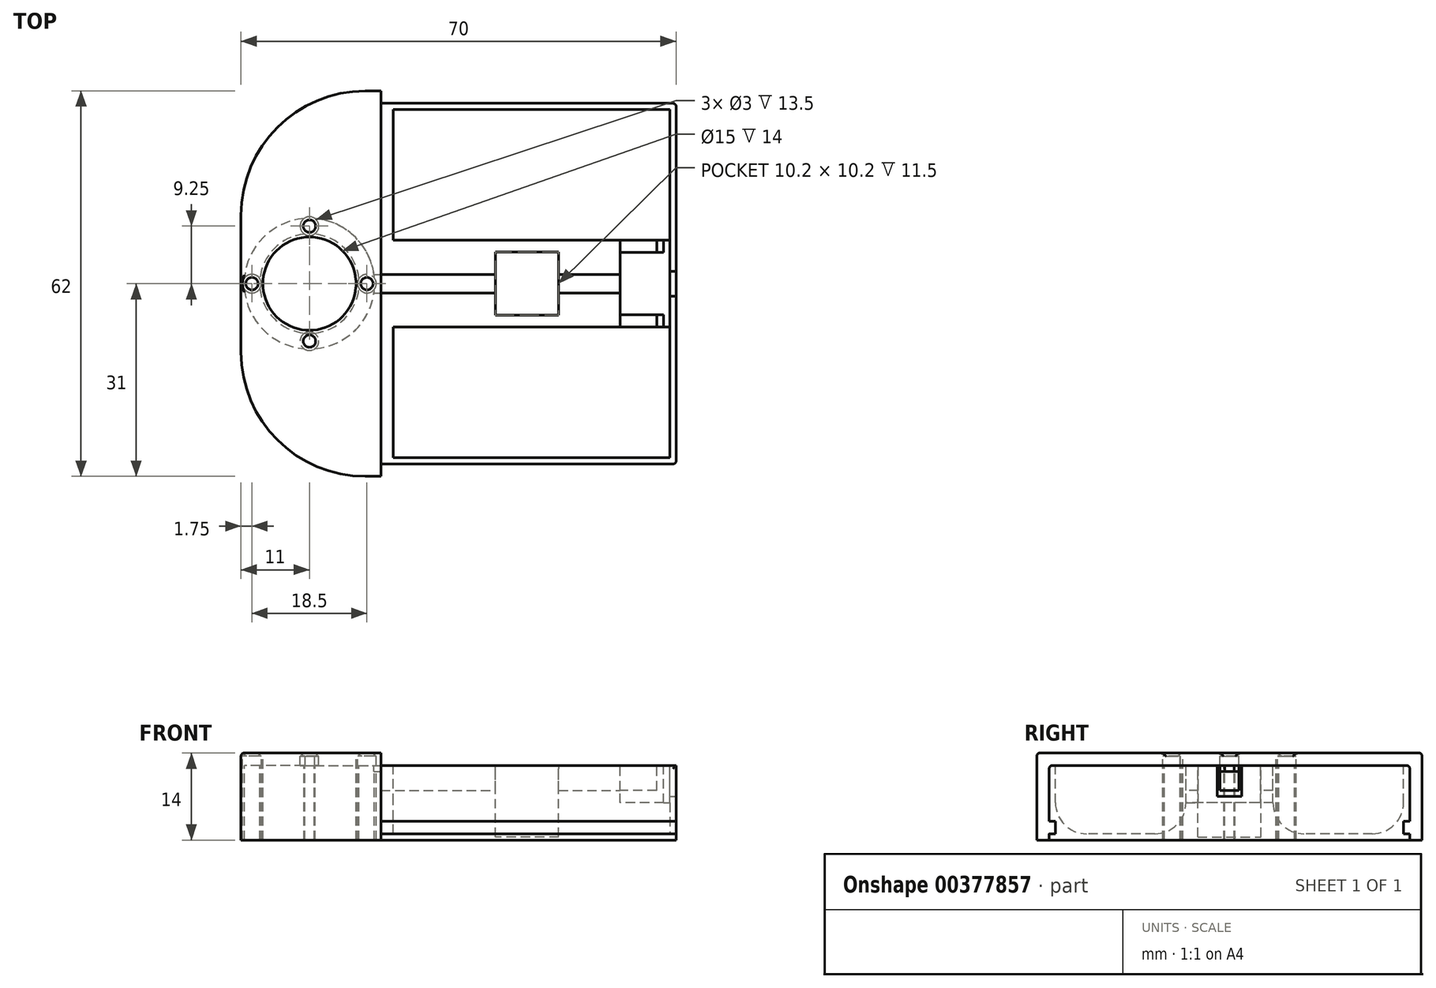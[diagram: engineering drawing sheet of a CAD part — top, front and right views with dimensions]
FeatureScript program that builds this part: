
annotation { "Feature Type Name" : "Feature", "Feature Type Description" : "" }
export const myFeature = defineFeature(function(context is Context, id is Id, definition is map)
    precondition{}
    {
        {
            var Q0;
            Q0=qCreatedBy(makeId("Top.planeOp"),FACE);
            var sketch = newSketch(context, id + "F0", { "sketchPlane" : qUnion([Q0])});
            skLineSegment(sketch, "E0.bottom", {"start": v(35, -29) * mm, "end": v(-35, -29) * mm});
            skLineSegment(sketch, "E0.top", {"start": v(35, 29) * mm, "end": v(-35, 29) * mm});
            skLineSegment(sketch, "E0.left", {"start": v(35, -29) * mm, "end": v(35, 29) * mm});
            skLineSegment(sketch, "E0.right", {"start": v(-35, -29) * mm, "end": v(-35, 29) * mm});
            skPoint(sketch, "E0.middle", {"position": v(0, 0) * mm});
            skLineSegment(sketch, "E1.bottom", {"start": v(-10.5, 28) * mm, "end": v(34, 28) * mm});
            skLineSegment(sketch, "E1.top", {"start": v(-10.5, 7) * mm, "end": v(34, 7) * mm});
            skLineSegment(sketch, "E1.left", {"start": v(-10.5, 28) * mm, "end": v(-10.5, 7) * mm});
            skLineSegment(sketch, "E1.right", {"start": v(34, 28) * mm, "end": v(34, 7) * mm});
            skLineSegment(sketch, "E2.bottom", {"start": v(-10.5, -7) * mm, "end": v(34, -7) * mm});
            skLineSegment(sketch, "E2.top", {"start": v(-10.5, -28) * mm, "end": v(34, -28) * mm});
            skLineSegment(sketch, "E2.left", {"start": v(-10.5, -7) * mm, "end": v(-10.5, -28) * mm});
            skLineSegment(sketch, "E2.right", {"start": v(34, -7) * mm, "end": v(34, -28) * mm});
            skPoint(sketch, "E3", {"position": v(-24, 0) * mm});
            skCircle(sketch, "E4", {"center": v(-24, 0) * mm, "radius": 7.5 * mm});
            skCircle(sketch, "E5", {"center": v(-24, 0) * mm, "radius": 8 * mm});
            skLineSegment(sketch, "E6", {"start": v(34, 7) * mm, "end": v(34, -7) * mm});
            skLineSegment(sketch, "E7", {"start": v(26, 7) * mm, "end": v(26, -7) * mm});
            skPoint(sketch, "E8", {"position": v(11, 0) * mm});
            skLineSegment(sketch, "E9.bottom", {"start": v(16.1, -5.1) * mm, "end": v(5.9, -5.1) * mm});
            skLineSegment(sketch, "E9.top", {"start": v(16.1, 5.1) * mm, "end": v(5.9, 5.1) * mm});
            skLineSegment(sketch, "E9.left", {"start": v(16.1, -5.1) * mm, "end": v(16.1, 5.1) * mm});
            skLineSegment(sketch, "E9.right", {"start": v(5.9, -5.1) * mm, "end": v(5.9, 5.1) * mm});
            skCircle(sketch, "E10", {"center": v(-24, 0) * mm, "radius": 9.25 * mm});
            skPoint(sketch, "E11", {"position": v(-14.75, 0) * mm});
            skPoint(sketch, "E12", {"position": v(-24, 9.25) * mm});
            skPoint(sketch, "E13", {"position": v(-33.25, 0) * mm});
            skPoint(sketch, "E14", {"position": v(-24, -9.25) * mm});
            skLineSegment(sketch, "E15", {"start": v(-24, -9.25) * mm, "end": v(-24, 0) * mm});
            skLineSegment(sketch, "E16", {"start": v(-24, 9.25) * mm, "end": v(-24, 0) * mm});
            skCircle(sketch, "E17", {"center": v(-24, 0) * mm, "radius": 10.5 * mm});
            skCircle(sketch, "E18", {"center": v(-24, 9.25) * mm, "radius": 1 * mm});
            skCircle(sketch, "E19", {"center": v(-14.75, 0) * mm, "radius": 1 * mm});
            skCircle(sketch, "E20", {"center": v(-33.25, 0) * mm, "radius": 1 * mm});
            skCircle(sketch, "E21", {"center": v(-24, -9.25) * mm, "radius": 1 * mm});
            skLineSegment(sketch, "E22", {"start": v(-35, 29) * mm, "end": v(-35, 31) * mm});
            skLineSegment(sketch, "E23", {"start": v(-35, 31) * mm, "end": v(-12.5, 31) * mm});
            skLineSegment(sketch, "E24", {"start": v(-12.5, 31) * mm, "end": v(-12.5, 29) * mm});
            skLineSegment(sketch, "E25", {"start": v(-35, -29) * mm, "end": v(-35, -31) * mm});
            skLineSegment(sketch, "E26", {"start": v(-35, -31) * mm, "end": v(-12.5, -31) * mm});
            skLineSegment(sketch, "E27", {"start": v(-12.5, -31) * mm, "end": v(-12.5, -29) * mm});
            skLineSegment(sketch, "E28", {"start": v(-12.5, -29) * mm, "end": v(-12.5, 29) * mm});
            skLineSegment(sketch, "E29", {"start": v(-13.6, -1.5) * mm, "end": v(26, -1.5) * mm});
            skLineSegment(sketch, "E30", {"start": v(-13.6, 1.5) * mm, "end": v(26, 1.5) * mm});
            skLineSegment(sketch, "E31", {"start": v(33, 7) * mm, "end": v(33, 5) * mm});
            skLineSegment(sketch, "E32", {"start": v(33, 5) * mm, "end": v(31.87, 5) * mm});
            skLineSegment(sketch, "E33", {"start": v(31.87, 5) * mm, "end": v(31.87, 7) * mm});
            skLineSegment(sketch, "E34", {"start": v(33, -7) * mm, "end": v(33, -5) * mm});
            skLineSegment(sketch, "E35", {"start": v(33, -5) * mm, "end": v(31.87, -5) * mm});
            skLineSegment(sketch, "E36", {"start": v(31.87, -5) * mm, "end": v(31.87, -7) * mm});
            skLineSegment(sketch, "E37", {"start": v(31.87, 5) * mm, "end": v(26, 5) * mm});
            skLineSegment(sketch, "E38", {"start": v(31.87, -5) * mm, "end": v(26, -5) * mm});
            skLineSegment(sketch, "E39", {"start": v(34, 2) * mm, "end": v(35, 2) * mm});
            skLineSegment(sketch, "E40", {"start": v(34, -2) * mm, "end": v(35, -2) * mm});
            skCircle(sketch, "E41", {"center": v(-24, -9.25) * mm, "radius": 1.5 * mm});
            skCircle(sketch, "E42", {"center": v(-33.25, 0) * mm, "radius": 1.5 * mm});
            skCircle(sketch, "E43", {"center": v(-14.75, 0) * mm, "radius": 1.5 * mm});
            skCircle(sketch, "E44", {"center": v(-24, 9.25) * mm, "radius": 1.5 * mm});
            skSolve(sketch);
        }
        {
            var Q0;
            Q0=makeQuery(id+"F0.imprint","IMPRINT",FACE,{"disambiguationData":[TD([[makeQuery(id+"F0.imprint","IMPRINT",EDGE,{"derivedFrom":sQuery(id+"F0.wireOp",EDGE,"E1.bottom")}),1.0]])]});
            var Q1;
            Q1=makeQuery(id+"F0.imprint","IMPRINT",FACE,{"disambiguationData":[TD([[makeQuery(id+"F0.imprint","IMPRINT",EDGE,{"derivedFrom":sQuery(id+"F0.wireOp",EDGE,"E1.bottom")}),-1.0]])]});
            var Q2;
            {var subQ0=sQuery(id+"F0.wireOp",EDGE,"E9.top");Q2=makeQuery(id+"F0.imprint","IMPRINT",FACE,{"disambiguationData":[TD([[makeQuery(id+"F0.imprint","IMPRINT",EDGE,{"derivedFrom":subQ0}),1.0]])]});}
            var Q3;
            {var subQ3=sQuery(id+"F0.wireOp",EDGE,"E33");Q3=makeQuery(id+"F0.imprint","IMPRINT",FACE,{"disambiguationData":[TD([[makeQuery(id+"F0.imprint","IMPRINT",EDGE,{"derivedFrom":subQ3}),1.0]])]});}
            var Q4;
            {var subQ0=sQuery(id+"F0.wireOp",EDGE,"E31");Q4=makeQuery(id+"F0.imprint","IMPRINT",FACE,{"disambiguationData":[TD([[makeQuery(id+"F0.imprint","IMPRINT",EDGE,{"derivedFrom":subQ0}),-1.0]])]});}
            var Q5;
            {var subQ9=sQuery(id+"F0.wireOp",EDGE,"E31");Q5=makeQuery(id+"F0.imprint","IMPRINT",FACE,{"disambiguationData":[TD([[makeQuery(id+"F0.imprint","IMPRINT",EDGE,{"derivedFrom":subQ9}),1.0]])]});}
            var Q6;
            Q6=makeQuery(id+"F0.imprint","IMPRINT",FACE,{"disambiguationData":[TD([[makeQuery(id+"F0.imprint","IMPRINT",EDGE,{"derivedFrom":sQuery(id+"F0.wireOp",EDGE,"E2.top")}),-1.0]])]});
            var Q7;
            {var subQ0=sQuery(id+"F0.wireOp",EDGE,"E39");Q7=makeQuery(id+"F0.imprint","IMPRINT",FACE,{"disambiguationData":[TD([[makeQuery(id+"F0.imprint","IMPRINT",EDGE,{"derivedFrom":subQ0}),-1.0]])]});}
            var Q8;
            {var subQ0=sQuery(id+"F0.wireOp",EDGE,"E34");Q8=makeQuery(id+"F0.imprint","IMPRINT",FACE,{"disambiguationData":[TD([[makeQuery(id+"F0.imprint","IMPRINT",EDGE,{"derivedFrom":subQ0}),1.0]])]});}
            var Q9;
            {var subQ3=sQuery(id+"F0.wireOp",EDGE,"E36");Q9=makeQuery(id+"F0.imprint","IMPRINT",FACE,{"disambiguationData":[TD([[makeQuery(id+"F0.imprint","IMPRINT",EDGE,{"derivedFrom":subQ3}),-1.0]])]});}
            var Q10;
            Q10=makeQuery(id+"F0.imprint","IMPRINT",FACE,{"disambiguationData":[TD([[makeQuery(id+"F0.imprint","IMPRINT",EDGE,{"derivedFrom":sQuery(id+"F0.wireOp",EDGE,"E2.top")}),1.0]])]});
            var Q11;
            {var subQ0=sQuery(id+"F0.wireOp",EDGE,"E9.bottom");Q11=makeQuery(id+"F0.imprint","IMPRINT",FACE,{"disambiguationData":[TD([[makeQuery(id+"F0.imprint","IMPRINT",EDGE,{"derivedFrom":subQ0}),-1.0]])]});}
            var Q12;
            {var subQ0=sQuery(id+"F0.wireOp",EDGE,"E29");var subQ1=sQuery(id+"F0.wireOp",EDGE,"E7");var subQ2=makeQuery(id+"F0.imprint","INTERSECT",VERTEX,{"derivedFrom":[subQ1,subQ0]});Q12=makeQuery(id+"F0.imprint","IMPRINT",FACE,{"disambiguationData":[TD([[makeQuery(id+"F0.imprint","IMPRINT",EDGE,{"disambiguationData":[TD([[subQ2,1.0]])],"derivedFrom":subQ1}),-1.0]])]});}
            var Q13;
            {var subQ0=sQuery(id+"F0.wireOp",EDGE,"E29");var subQ1=sQuery(id+"F0.wireOp",EDGE,"E9.right");var subQ2=makeQuery(id+"F0.imprint","INTERSECT",VERTEX,{"derivedFrom":[subQ1,subQ0]});Q13=makeQuery(id+"F0.imprint","IMPRINT",FACE,{"disambiguationData":[TD([[makeQuery(id+"F0.imprint","IMPRINT",EDGE,{"disambiguationData":[TD([[subQ2,-1.0]])],"derivedFrom":subQ1}),1.0]])]});}
            var Q14;
            {var subQ0=sQuery(id+"F0.wireOp",EDGE,"E29");var subQ1=sQuery(id+"F0.wireOp",EDGE,"E9.left");var subQ2=makeQuery(id+"F0.imprint","INTERSECT",VERTEX,{"derivedFrom":[subQ1,subQ0]});Q14=makeQuery(id+"F0.imprint","IMPRINT",FACE,{"disambiguationData":[TD([[makeQuery(id+"F0.imprint","IMPRINT",EDGE,{"disambiguationData":[TD([[subQ2,-1.0]])],"derivedFrom":subQ1}),1.0]])]});}
            var Q15;
            {var subQ5=sQuery(id+"F0.wireOp",EDGE,"E0.right");Q15=makeQuery(id+"F0.imprint","IMPRINT",FACE,{"disambiguationData":[TD([[makeQuery(id+"F0.imprint","IMPRINT",EDGE,{"derivedFrom":subQ5}),-1.0]])]});}
            var Q16;
            {var subQ0=sQuery(id+"F0.wireOp",EDGE,"E22");Q16=makeQuery(id+"F0.imprint","IMPRINT",FACE,{"disambiguationData":[TD([[makeQuery(id+"F0.imprint","IMPRINT",EDGE,{"derivedFrom":subQ0}),-1.0]])]});}
            var Q17;
            {var subQ0=sQuery(id+"F0.wireOp",EDGE,"E25");Q17=makeQuery(id+"F0.imprint","IMPRINT",FACE,{"disambiguationData":[TD([[makeQuery(id+"F0.imprint","IMPRINT",EDGE,{"derivedFrom":subQ0}),1.0]])]});}
            var Q18;
            {var subQ0=sQuery(id+"F0.wireOp",EDGE,"E15");var subQ1=sQuery(id+"F0.wireOp",EDGE,"E4");var subQ2=makeQuery(id+"F0.imprint","INTERSECT",VERTEX,{"derivedFrom":[subQ1,subQ0]});Q18=makeQuery(id+"F0.imprint","IMPRINT",FACE,{"disambiguationData":[TD([[makeQuery(id+"F0.imprint","IMPRINT",EDGE,{"disambiguationData":[TD([[subQ2,-1.0]])],"derivedFrom":subQ1}),-1.0]])]});}
            var Q19;
            {var subQ0=sQuery(id+"F0.wireOp",EDGE,"E15");var subQ1=sQuery(id+"F0.wireOp",EDGE,"E4");var subQ2=makeQuery(id+"F0.imprint","INTERSECT",VERTEX,{"derivedFrom":[subQ1,subQ0]});Q19=makeQuery(id+"F0.imprint","IMPRINT",FACE,{"disambiguationData":[TD([[makeQuery(id+"F0.imprint","IMPRINT",EDGE,{"disambiguationData":[TD([[subQ2,1.0]])],"derivedFrom":subQ1}),-1.0]])]});}
            var Q20;
            {var subQ0=sQuery(id+"F0.wireOp",EDGE,"E29");var subQ1=sQuery(id+"F0.wireOp",EDGE,"E17");var subQ2=makeQuery(id+"F0.imprint","INTERSECT",VERTEX,{"derivedFrom":[subQ1,subQ0]});Q20=makeQuery(id+"F0.imprint","IMPRINT",FACE,{"disambiguationData":[TD([[makeQuery(id+"F0.imprint","IMPRINT",EDGE,{"disambiguationData":[TD([[subQ2,-1.0]])],"derivedFrom":subQ1}),-1.0]])]});}
            extrude(context, id + "F1", {"entities" : qUnion([Q0, Q1, Q2, Q3, Q4, Q5, Q6, Q7, Q8, Q9, Q10, Q11, Q12, Q13, Q14, Q15, Q16, Q17, Q18, Q19, Q20]), "oppositeDirection" : true, "depth" : 12 * mm});
        }
        {
            var Q0;
            {var subQ1=sQuery(id+"F0.wireOp",EDGE,"E17");var subQ5=sQuery(id+"F0.wireOp",EDGE,"E30");var subQ9=makeQuery(id+"F0.imprint","INTERSECT",VERTEX,{"derivedFrom":[subQ1,subQ5]});Q0=makeQuery(id+"F0.imprint","IMPRINT",FACE,{"disambiguationData":[TD([[makeQuery(id+"F0.imprint","IMPRINT",EDGE,{"disambiguationData":[TD([[subQ9,1.0]])],"derivedFrom":subQ1}),-1.0]])]});}
            extrude(context, id + "F2", {"entities" : qUnion([Q0]), "operationType" : NewBodyOperationType.REMOVE, "oppositeDirection" : true, "depth" : 1 * mm});
        }
        {
            var Q0;
            {var subQ0=sQuery(id+"F0.wireOp",EDGE,"E22");Q0=makeQuery(id+"F0.imprint","IMPRINT",FACE,{"disambiguationData":[TD([[makeQuery(id+"F0.imprint","IMPRINT",EDGE,{"derivedFrom":subQ0}),-1.0]])]});}
            var Q1;
            {var subQ5=sQuery(id+"F0.wireOp",EDGE,"E0.right");Q1=makeQuery(id+"F0.imprint","IMPRINT",FACE,{"disambiguationData":[TD([[makeQuery(id+"F0.imprint","IMPRINT",EDGE,{"derivedFrom":subQ5}),-1.0]])]});}
            var Q2;
            {var subQ0=sQuery(id+"F0.wireOp",EDGE,"E25");Q2=makeQuery(id+"F0.imprint","IMPRINT",FACE,{"disambiguationData":[TD([[makeQuery(id+"F0.imprint","IMPRINT",EDGE,{"derivedFrom":subQ0}),1.0]])]});}
            var Q3;
            {var subQ0=sQuery(id+"F0.wireOp",EDGE,"E29");var subQ1=sQuery(id+"F0.wireOp",EDGE,"E17");var subQ2=makeQuery(id+"F0.imprint","INTERSECT",VERTEX,{"derivedFrom":[subQ1,subQ0]});Q3=makeQuery(id+"F0.imprint","IMPRINT",FACE,{"disambiguationData":[TD([[makeQuery(id+"F0.imprint","IMPRINT",EDGE,{"disambiguationData":[TD([[subQ2,-1.0]])],"derivedFrom":subQ1}),-1.0]])]});}
            var Q4;
            {var subQ0=sQuery(id+"F0.wireOp",EDGE,"E44");var subQ1=sQuery(id+"F0.wireOp",EDGE,"E5");var subQ2=makeQuery(id+"F0.imprint","INTERSECT",VERTEX,{"disambiguationData":[OD(1.0)],"derivedFrom":[subQ1,subQ0]});Q4=makeQuery(id+"F0.imprint","IMPRINT",FACE,{"disambiguationData":[TD([[makeQuery(id+"F0.imprint","IMPRINT",EDGE,{"disambiguationData":[TD([[subQ2,-1.0]])],"derivedFrom":subQ1}),-1.0]])]});}
            var Q5;
            {var subQ0=sQuery(id+"F0.wireOp",EDGE,"E44");var subQ1=sQuery(id+"F0.wireOp",EDGE,"E10");var subQ2=makeQuery(id+"F0.imprint","INTERSECT",VERTEX,{"disambiguationData":[OD(1.0)],"derivedFrom":[subQ1,subQ0]});Q5=makeQuery(id+"F0.imprint","IMPRINT",FACE,{"disambiguationData":[TD([[makeQuery(id+"F0.imprint","IMPRINT",EDGE,{"disambiguationData":[TD([[subQ2,-1.0]])],"derivedFrom":subQ1}),-1.0]])]});}
            var Q6;
            {var subQ4=sQuery(id+"F0.wireOp",EDGE,"E43");var subQ5=sQuery(id+"F0.wireOp",EDGE,"E10");var subQ6=makeQuery(id+"F0.imprint","INTERSECT",VERTEX,{"disambiguationData":[OD(0.0)],"derivedFrom":[subQ5,subQ4]});Q6=makeQuery(id+"F0.imprint","IMPRINT",FACE,{"disambiguationData":[TD([[makeQuery(id+"F0.imprint","IMPRINT",EDGE,{"disambiguationData":[TD([[subQ6,-1.0]])],"derivedFrom":subQ5}),-1.0]])]});}
            var Q7;
            {var subQ0=sQuery(id+"F0.wireOp",EDGE,"E44");var subQ1=sQuery(id+"F0.wireOp",EDGE,"E5");var subQ2=makeQuery(id+"F0.imprint","INTERSECT",VERTEX,{"disambiguationData":[OD(0.0)],"derivedFrom":[subQ1,subQ0]});Q7=makeQuery(id+"F0.imprint","IMPRINT",FACE,{"disambiguationData":[TD([[makeQuery(id+"F0.imprint","IMPRINT",EDGE,{"disambiguationData":[TD([[subQ2,1.0]])],"derivedFrom":subQ1}),-1.0]])]});}
            var Q8;
            {var subQ0=sQuery(id+"F0.wireOp",EDGE,"E41");var subQ1=sQuery(id+"F0.wireOp",EDGE,"E5");var subQ2=makeQuery(id+"F0.imprint","INTERSECT",VERTEX,{"disambiguationData":[OD(1.0)],"derivedFrom":[subQ1,subQ0]});Q8=makeQuery(id+"F0.imprint","IMPRINT",FACE,{"disambiguationData":[TD([[makeQuery(id+"F0.imprint","IMPRINT",EDGE,{"disambiguationData":[TD([[subQ2,-1.0]])],"derivedFrom":subQ1}),-1.0]])]});}
            var Q9;
            {var subQ0=sQuery(id+"F0.wireOp",EDGE,"E41");var subQ1=sQuery(id+"F0.wireOp",EDGE,"E10");var subQ2=makeQuery(id+"F0.imprint","INTERSECT",VERTEX,{"disambiguationData":[OD(1.0)],"derivedFrom":[subQ1,subQ0]});Q9=makeQuery(id+"F0.imprint","IMPRINT",FACE,{"disambiguationData":[TD([[makeQuery(id+"F0.imprint","IMPRINT",EDGE,{"disambiguationData":[TD([[subQ2,-1.0]])],"derivedFrom":subQ1}),-1.0]])]});}
            var Q10;
            {var subQ0=sQuery(id+"F0.wireOp",EDGE,"E42");var subQ1=sQuery(id+"F0.wireOp",EDGE,"E10");var subQ2=makeQuery(id+"F0.imprint","INTERSECT",VERTEX,{"disambiguationData":[OD(1.0)],"derivedFrom":[subQ1,subQ0]});Q10=makeQuery(id+"F0.imprint","IMPRINT",FACE,{"disambiguationData":[TD([[makeQuery(id+"F0.imprint","IMPRINT",EDGE,{"disambiguationData":[TD([[subQ2,-1.0]])],"derivedFrom":subQ1}),-1.0]])]});}
            var Q11;
            {var subQ0=sQuery(id+"F0.wireOp",EDGE,"E42");var subQ1=sQuery(id+"F0.wireOp",EDGE,"E5");var subQ2=makeQuery(id+"F0.imprint","INTERSECT",VERTEX,{"disambiguationData":[OD(1.0)],"derivedFrom":[subQ1,subQ0]});Q11=makeQuery(id+"F0.imprint","IMPRINT",FACE,{"disambiguationData":[TD([[makeQuery(id+"F0.imprint","IMPRINT",EDGE,{"disambiguationData":[TD([[subQ2,-1.0]])],"derivedFrom":subQ1}),-1.0]])]});}
            var Q12;
            {var subQ0=sQuery(id+"F0.wireOp",EDGE,"E15");var subQ1=sQuery(id+"F0.wireOp",EDGE,"E4");var subQ2=makeQuery(id+"F0.imprint","INTERSECT",VERTEX,{"derivedFrom":[subQ1,subQ0]});Q12=makeQuery(id+"F0.imprint","IMPRINT",FACE,{"disambiguationData":[TD([[makeQuery(id+"F0.imprint","IMPRINT",EDGE,{"disambiguationData":[TD([[subQ2,1.0]])],"derivedFrom":subQ1}),-1.0]])]});}
            var Q13;
            {var subQ0=sQuery(id+"F0.wireOp",EDGE,"E15");var subQ1=sQuery(id+"F0.wireOp",EDGE,"E4");var subQ2=makeQuery(id+"F0.imprint","INTERSECT",VERTEX,{"derivedFrom":[subQ1,subQ0]});Q13=makeQuery(id+"F0.imprint","IMPRINT",FACE,{"disambiguationData":[TD([[makeQuery(id+"F0.imprint","IMPRINT",EDGE,{"disambiguationData":[TD([[subQ2,-1.0]])],"derivedFrom":subQ1}),-1.0]])]});}
            extrude(context, id + "F3", {"entities" : qUnion([Q0, Q1, Q2, Q3, Q4, Q5, Q6, Q7, Q8, Q9, Q10, Q11, Q12, Q13]), "depth" : 2 * mm});
        }
        {
            var Q0;
            Q0=makeQuery(id+"F1.opExtrude","SWEPT_EDGE",EDGE,{"disambiguationData":[OSD([sQuery(id+"F0.wireOp",EDGE,"E22"),sQuery(id+"F0.wireOp",EDGE,"E23")])]});
            var Q1;
            Q1=makeQuery(id+"F1.opExtrude","SWEPT_EDGE",EDGE,{"disambiguationData":[OSD([sQuery(id+"F0.wireOp",EDGE,"E25"),sQuery(id+"F0.wireOp",EDGE,"E26")])]});
            var Q2;
            Q2=makeQuery(id+"F3.opExtrude","SWEPT_EDGE",EDGE,{"disambiguationData":[OSD([sQuery(id+"F0.wireOp",EDGE,"E25"),sQuery(id+"F0.wireOp",EDGE,"E26")])]});
            var Q3;
            Q3=makeQuery(id+"F3.opExtrude","SWEPT_EDGE",EDGE,{"disambiguationData":[OSD([sQuery(id+"F0.wireOp",EDGE,"E22"),sQuery(id+"F0.wireOp",EDGE,"E23")])]});
            fillet(context, id + "F4", {"entities" : qUnion([Q0, Q1, Q2, Q3]), "radius" : 20 * mm, "tangentPropagation" : true, "allowEdgeOverflow" : false});
        }
        {
            var Q0;
            Q0=makeQuery(id+"F0.imprint","IMPRINT",FACE,{"disambiguationData":[TD([[makeQuery(id+"F0.imprint","IMPRINT",EDGE,{"derivedFrom":sQuery(id+"F0.wireOp",EDGE,"E1.bottom")}),-1.0]])]});
            var Q1;
            Q1=makeQuery(id+"F0.imprint","IMPRINT",FACE,{"disambiguationData":[TD([[makeQuery(id+"F0.imprint","IMPRINT",EDGE,{"derivedFrom":sQuery(id+"F0.wireOp",EDGE,"E2.top")}),1.0]])]});
            extrude(context, id + "F5", {"entities" : qUnion([Q0, Q1]), "operationType" : NewBodyOperationType.REMOVE, "oppositeDirection" : true, "depth" : 11 * mm});
        }
        {
            var Q0;
            Q0=makeQuery(id+"F5.boolean.opBoolean","COPY",EDGE,{"derivedFrom":makeQuery(id+"F5.opExtrude","CAP_EDGE",EDGE,{"disambiguationData":[OSD([sQuery(id+"F0.wireOp",EDGE,"E2.bottom")])],"isStart":false})});
            var Q1;
            Q1=makeQuery(id+"F5.boolean.opBoolean","COPY",EDGE,{"derivedFrom":makeQuery(id+"F5.opExtrude","CAP_EDGE",EDGE,{"disambiguationData":[OSD([sQuery(id+"F0.wireOp",EDGE,"E2.top")])],"isStart":false})});
            var Q2;
            Q2=makeQuery(id+"F5.boolean.opBoolean","COPY",EDGE,{"derivedFrom":makeQuery(id+"F5.opExtrude","CAP_EDGE",EDGE,{"disambiguationData":[OSD([sQuery(id+"F0.wireOp",EDGE,"E1.top")])],"isStart":false})});
            var Q3;
            Q3=makeQuery(id+"F5.boolean.opBoolean","COPY",EDGE,{"derivedFrom":makeQuery(id+"F5.opExtrude","CAP_EDGE",EDGE,{"disambiguationData":[OSD([sQuery(id+"F0.wireOp",EDGE,"E1.bottom")])],"isStart":false})});
            fillet(context, id + "F6", {"entities" : qUnion([Q0, Q1, Q2, Q3]), "radius" : 5 * mm, "tangentPropagation" : true, "allowEdgeOverflow" : false});
        }
        {
            var Q0;
            {var subQ0=sQuery(id+"F0.wireOp",EDGE,"E9.bottom");Q0=makeQuery(id+"F0.imprint","IMPRINT",FACE,{"disambiguationData":[TD([[makeQuery(id+"F0.imprint","IMPRINT",EDGE,{"derivedFrom":subQ0}),-1.0]])]});}
            var Q1;
            {var subQ0=sQuery(id+"F0.wireOp",EDGE,"E29");var subQ1=sQuery(id+"F0.wireOp",EDGE,"E9.left");var subQ2=makeQuery(id+"F0.imprint","INTERSECT",VERTEX,{"derivedFrom":[subQ1,subQ0]});Q1=makeQuery(id+"F0.imprint","IMPRINT",FACE,{"disambiguationData":[TD([[makeQuery(id+"F0.imprint","IMPRINT",EDGE,{"disambiguationData":[TD([[subQ2,-1.0]])],"derivedFrom":subQ1}),1.0]])]});}
            var Q2;
            {var subQ0=sQuery(id+"F0.wireOp",EDGE,"E9.top");Q2=makeQuery(id+"F0.imprint","IMPRINT",FACE,{"disambiguationData":[TD([[makeQuery(id+"F0.imprint","IMPRINT",EDGE,{"derivedFrom":subQ0}),1.0]])]});}
            extrude(context, id + "F7", {"entities" : qUnion([Q0, Q1, Q2]), "operationType" : NewBodyOperationType.REMOVE, "oppositeDirection" : true, "depth" : 11.5 * mm});
        }
        {
            var Q0;
            {var subQ9=sQuery(id+"F0.wireOp",EDGE,"E31");Q0=makeQuery(id+"F0.imprint","IMPRINT",FACE,{"disambiguationData":[TD([[makeQuery(id+"F0.imprint","IMPRINT",EDGE,{"derivedFrom":subQ9}),1.0]])]});}
            extrude(context, id + "F8", {"entities" : qUnion([Q0]), "operationType" : NewBodyOperationType.REMOVE, "oppositeDirection" : true, "depth" : 6 * mm});
        }
        {
            var Q0;
            {var subQ0=sQuery(id+"F0.wireOp",EDGE,"E29");var subQ1=sQuery(id+"F0.wireOp",EDGE,"E9.right");var subQ2=makeQuery(id+"F0.imprint","INTERSECT",VERTEX,{"derivedFrom":[subQ1,subQ0]});Q0=makeQuery(id+"F0.imprint","IMPRINT",FACE,{"disambiguationData":[TD([[makeQuery(id+"F0.imprint","IMPRINT",EDGE,{"disambiguationData":[TD([[subQ2,-1.0]])],"derivedFrom":subQ1}),1.0]])]});}
            var Q1;
            {var subQ0=sQuery(id+"F0.wireOp",EDGE,"E29");var subQ1=sQuery(id+"F0.wireOp",EDGE,"E7");var subQ2=makeQuery(id+"F0.imprint","INTERSECT",VERTEX,{"derivedFrom":[subQ1,subQ0]});Q1=makeQuery(id+"F0.imprint","IMPRINT",FACE,{"disambiguationData":[TD([[makeQuery(id+"F0.imprint","IMPRINT",EDGE,{"disambiguationData":[TD([[subQ2,1.0]])],"derivedFrom":subQ1}),-1.0]])]});}
            var Q2;
            {var subQ3=sQuery(id+"F0.wireOp",EDGE,"E33");Q2=makeQuery(id+"F0.imprint","IMPRINT",FACE,{"disambiguationData":[TD([[makeQuery(id+"F0.imprint","IMPRINT",EDGE,{"derivedFrom":subQ3}),1.0]])]});}
            var Q3;
            {var subQ3=sQuery(id+"F0.wireOp",EDGE,"E36");Q3=makeQuery(id+"F0.imprint","IMPRINT",FACE,{"disambiguationData":[TD([[makeQuery(id+"F0.imprint","IMPRINT",EDGE,{"derivedFrom":subQ3}),-1.0]])]});}
            extrude(context, id + "F9", {"entities" : qUnion([Q0, Q1, Q2, Q3]), "operationType" : NewBodyOperationType.REMOVE, "oppositeDirection" : true, "depth" : 4 * mm});
        }
        {
            var Q0;
            {var subQ0=sQuery(id+"F0.wireOp",EDGE,"E42");var subQ1=sQuery(id+"F0.wireOp",EDGE,"E17");var subQ2=makeQuery(id+"F0.imprint","INTERSECT",VERTEX,{"disambiguationData":[OD(0.0)],"derivedFrom":[subQ1,subQ0]});Q0=makeQuery(id+"F0.imprint","IMPRINT",FACE,{"disambiguationData":[TD([[makeQuery(id+"F0.imprint","IMPRINT",EDGE,{"disambiguationData":[TD([[subQ2,-1.0]])],"derivedFrom":subQ1}),-1.0]])]});}
            var Q1;
            {var subQ1=sQuery(id+"F0.wireOp",EDGE,"E10");var subQ4=sQuery(id+"F0.wireOp",EDGE,"E42");var subQ9=makeQuery(id+"F0.imprint","INTERSECT",VERTEX,{"disambiguationData":[OD(0.0)],"derivedFrom":[subQ1,subQ4]});Q1=makeQuery(id+"F0.imprint","IMPRINT",FACE,{"disambiguationData":[TD([[makeQuery(id+"F0.imprint","IMPRINT",EDGE,{"disambiguationData":[TD([[subQ9,-1.0]])],"derivedFrom":subQ1}),-1.0]])]});}
            var Q2;
            {var subQ4=sQuery(id+"F0.wireOp",EDGE,"E42");var subQ5=sQuery(id+"F0.wireOp",EDGE,"E5");var subQ6=makeQuery(id+"F0.imprint","INTERSECT",VERTEX,{"disambiguationData":[OD(0.0)],"derivedFrom":[subQ5,subQ4]});Q2=makeQuery(id+"F0.imprint","IMPRINT",FACE,{"disambiguationData":[TD([[makeQuery(id+"F0.imprint","IMPRINT",EDGE,{"disambiguationData":[TD([[subQ6,-1.0]])],"derivedFrom":subQ5}),-1.0]])]});}
            var Q3;
            {var subQ0=sQuery(id+"F0.wireOp",EDGE,"E42");var subQ1=sQuery(id+"F0.wireOp",EDGE,"E5");var subQ2=makeQuery(id+"F0.imprint","INTERSECT",VERTEX,{"disambiguationData":[OD(0.0)],"derivedFrom":[subQ1,subQ0]});Q3=makeQuery(id+"F0.imprint","IMPRINT",FACE,{"disambiguationData":[TD([[makeQuery(id+"F0.imprint","IMPRINT",EDGE,{"disambiguationData":[TD([[subQ2,-1.0]])],"derivedFrom":subQ1}),1.0]])]});}
            var Q4;
            {var subQ0=sQuery(id+"F0.wireOp",EDGE,"E43");var subQ1=sQuery(id+"F0.wireOp",EDGE,"E5");var subQ2=makeQuery(id+"F0.imprint","INTERSECT",VERTEX,{"disambiguationData":[OD(0.0)],"derivedFrom":[subQ1,subQ0]});Q4=makeQuery(id+"F0.imprint","IMPRINT",FACE,{"disambiguationData":[TD([[makeQuery(id+"F0.imprint","IMPRINT",EDGE,{"disambiguationData":[TD([[subQ2,1.0]])],"derivedFrom":subQ1}),1.0]])]});}
            var Q5;
            {var subQ4=sQuery(id+"F0.wireOp",EDGE,"E43");var subQ6=sQuery(id+"F0.wireOp",EDGE,"E5");var subQ7=makeQuery(id+"F0.imprint","INTERSECT",VERTEX,{"disambiguationData":[OD(0.0)],"derivedFrom":[subQ6,subQ4]});Q5=makeQuery(id+"F0.imprint","IMPRINT",FACE,{"disambiguationData":[TD([[makeQuery(id+"F0.imprint","IMPRINT",EDGE,{"disambiguationData":[TD([[subQ7,1.0]])],"derivedFrom":subQ6}),-1.0]])]});}
            var Q6;
            {var subQ1=sQuery(id+"F0.wireOp",EDGE,"E10");var subQ4=sQuery(id+"F0.wireOp",EDGE,"E43");var subQ9=makeQuery(id+"F0.imprint","INTERSECT",VERTEX,{"disambiguationData":[OD(0.0)],"derivedFrom":[subQ1,subQ4]});Q6=makeQuery(id+"F0.imprint","IMPRINT",FACE,{"disambiguationData":[TD([[makeQuery(id+"F0.imprint","IMPRINT",EDGE,{"disambiguationData":[TD([[subQ9,1.0]])],"derivedFrom":subQ1}),-1.0]])]});}
            var Q7;
            {var subQ0=sQuery(id+"F0.wireOp",EDGE,"E43");var subQ1=sQuery(id+"F0.wireOp",EDGE,"E17");var subQ2=makeQuery(id+"F0.imprint","INTERSECT",VERTEX,{"disambiguationData":[OD(0.0)],"derivedFrom":[subQ1,subQ0]});Q7=makeQuery(id+"F0.imprint","IMPRINT",FACE,{"disambiguationData":[TD([[makeQuery(id+"F0.imprint","IMPRINT",EDGE,{"disambiguationData":[TD([[subQ2,1.0]])],"derivedFrom":subQ1}),-1.0]])]});}
            var Q8;
            {var subQ0=sQuery(id+"F0.wireOp",EDGE,"E41");var subQ1=sQuery(id+"F0.wireOp",EDGE,"E5");var subQ2=makeQuery(id+"F0.imprint","INTERSECT",VERTEX,{"disambiguationData":[OD(0.0)],"derivedFrom":[subQ1,subQ0]});Q8=makeQuery(id+"F0.imprint","IMPRINT",FACE,{"disambiguationData":[TD([[makeQuery(id+"F0.imprint","IMPRINT",EDGE,{"disambiguationData":[TD([[subQ2,-1.0]])],"derivedFrom":subQ1}),1.0]])]});}
            var Q9;
            {var subQ0=sQuery(id+"F0.wireOp",EDGE,"E15");var subQ1=sQuery(id+"F0.wireOp",EDGE,"E5");var subQ2=makeQuery(id+"F0.imprint","INTERSECT",VERTEX,{"derivedFrom":[subQ1,subQ0]});Q9=makeQuery(id+"F0.imprint","IMPRINT",FACE,{"disambiguationData":[TD([[makeQuery(id+"F0.imprint","IMPRINT",EDGE,{"disambiguationData":[TD([[subQ2,-1.0]])],"derivedFrom":subQ1}),1.0]])]});}
            var Q10;
            {var subQ3=sQuery(id+"F0.wireOp",EDGE,"E15");var subQ5=sQuery(id+"F0.wireOp",EDGE,"E5");var subQ6=makeQuery(id+"F0.imprint","INTERSECT",VERTEX,{"derivedFrom":[subQ5,subQ3]});Q10=makeQuery(id+"F0.imprint","IMPRINT",FACE,{"disambiguationData":[TD([[makeQuery(id+"F0.imprint","IMPRINT",EDGE,{"disambiguationData":[TD([[subQ6,-1.0]])],"derivedFrom":subQ5}),-1.0]])]});}
            var Q11;
            {var subQ0=sQuery(id+"F0.wireOp",EDGE,"E41");var subQ1=sQuery(id+"F0.wireOp",EDGE,"E17");var subQ2=makeQuery(id+"F0.imprint","INTERSECT",VERTEX,{"disambiguationData":[OD(0.0)],"derivedFrom":[subQ1,subQ0]});Q11=makeQuery(id+"F0.imprint","IMPRINT",FACE,{"disambiguationData":[TD([[makeQuery(id+"F0.imprint","IMPRINT",EDGE,{"disambiguationData":[TD([[subQ2,-1.0]])],"derivedFrom":subQ1}),-1.0]])]});}
            var Q12;
            {var subQ1=sQuery(id+"F0.wireOp",EDGE,"E10");var subQ4=sQuery(id+"F0.wireOp",EDGE,"E41");var subQ9=makeQuery(id+"F0.imprint","INTERSECT",VERTEX,{"disambiguationData":[OD(0.0)],"derivedFrom":[subQ1,subQ4]});Q12=makeQuery(id+"F0.imprint","IMPRINT",FACE,{"disambiguationData":[TD([[makeQuery(id+"F0.imprint","IMPRINT",EDGE,{"disambiguationData":[TD([[subQ9,-1.0]])],"derivedFrom":subQ1}),-1.0]])]});}
            var Q13;
            {var subQ1=sQuery(id+"F0.wireOp",EDGE,"E5");var subQ7=sQuery(id+"F0.wireOp",EDGE,"E41");var subQ8=makeQuery(id+"F0.imprint","INTERSECT",VERTEX,{"disambiguationData":[OD(0.0)],"derivedFrom":[subQ1,subQ7]});Q13=makeQuery(id+"F0.imprint","IMPRINT",FACE,{"disambiguationData":[TD([[makeQuery(id+"F0.imprint","IMPRINT",EDGE,{"disambiguationData":[TD([[subQ8,-1.0]])],"derivedFrom":subQ1}),-1.0]])]});}
            var Q14;
            {var subQ0=sQuery(id+"F0.wireOp",EDGE,"E44");var subQ1=sQuery(id+"F0.wireOp",EDGE,"E5");var subQ2=makeQuery(id+"F0.imprint","INTERSECT",VERTEX,{"disambiguationData":[OD(0.0)],"derivedFrom":[subQ1,subQ0]});Q14=makeQuery(id+"F0.imprint","IMPRINT",FACE,{"disambiguationData":[TD([[makeQuery(id+"F0.imprint","IMPRINT",EDGE,{"disambiguationData":[TD([[subQ2,-1.0]])],"derivedFrom":subQ1}),1.0]])]});}
            var Q15;
            {var subQ0=sQuery(id+"F0.wireOp",EDGE,"E16");var subQ1=sQuery(id+"F0.wireOp",EDGE,"E5");var subQ2=makeQuery(id+"F0.imprint","INTERSECT",VERTEX,{"derivedFrom":[subQ1,subQ0]});Q15=makeQuery(id+"F0.imprint","IMPRINT",FACE,{"disambiguationData":[TD([[makeQuery(id+"F0.imprint","IMPRINT",EDGE,{"disambiguationData":[TD([[subQ2,-1.0]])],"derivedFrom":subQ1}),1.0]])]});}
            var Q16;
            {var subQ3=sQuery(id+"F0.wireOp",EDGE,"E16");var subQ7=sQuery(id+"F0.wireOp",EDGE,"E5");var subQ8=makeQuery(id+"F0.imprint","INTERSECT",VERTEX,{"derivedFrom":[subQ7,subQ3]});Q16=makeQuery(id+"F0.imprint","IMPRINT",FACE,{"disambiguationData":[TD([[makeQuery(id+"F0.imprint","IMPRINT",EDGE,{"disambiguationData":[TD([[subQ8,-1.0]])],"derivedFrom":subQ7}),-1.0]])]});}
            var Q17;
            {var subQ1=sQuery(id+"F0.wireOp",EDGE,"E10");var subQ4=sQuery(id+"F0.wireOp",EDGE,"E44");var subQ9=makeQuery(id+"F0.imprint","INTERSECT",VERTEX,{"disambiguationData":[OD(0.0)],"derivedFrom":[subQ1,subQ4]});Q17=makeQuery(id+"F0.imprint","IMPRINT",FACE,{"disambiguationData":[TD([[makeQuery(id+"F0.imprint","IMPRINT",EDGE,{"disambiguationData":[TD([[subQ9,-1.0]])],"derivedFrom":subQ1}),-1.0]])]});}
            var Q18;
            {var subQ0=sQuery(id+"F0.wireOp",EDGE,"E44");var subQ1=sQuery(id+"F0.wireOp",EDGE,"E17");var subQ2=makeQuery(id+"F0.imprint","INTERSECT",VERTEX,{"disambiguationData":[OD(0.0)],"derivedFrom":[subQ1,subQ0]});Q18=makeQuery(id+"F0.imprint","IMPRINT",FACE,{"disambiguationData":[TD([[makeQuery(id+"F0.imprint","IMPRINT",EDGE,{"disambiguationData":[TD([[subQ2,-1.0]])],"derivedFrom":subQ1}),-1.0]])]});}
            var Q19;
            {var subQ5=sQuery(id+"F0.wireOp",EDGE,"E5");var subQ7=sQuery(id+"F0.wireOp",EDGE,"E44");var subQ9=makeQuery(id+"F0.imprint","INTERSECT",VERTEX,{"disambiguationData":[OD(0.0)],"derivedFrom":[subQ5,subQ7]});Q19=makeQuery(id+"F0.imprint","IMPRINT",FACE,{"disambiguationData":[TD([[makeQuery(id+"F0.imprint","IMPRINT",EDGE,{"disambiguationData":[TD([[subQ9,-1.0]])],"derivedFrom":subQ5}),-1.0]])]});}
            extrude(context, id + "F10", {"entities" : qUnion([Q0, Q1, Q2, Q3, Q4, Q5, Q6, Q7, Q8, Q9, Q10, Q11, Q12, Q13, Q14, Q15, Q16, Q17, Q18, Q19]), "operationType" : NewBodyOperationType.ADD, "depth" : 2 * mm});
        }
        {
            var Q0;
            {var subQ1=sQuery(id+"F0.wireOp",EDGE,"E10");var subQ4=sQuery(id+"F0.wireOp",EDGE,"E41");var subQ9=makeQuery(id+"F0.imprint","INTERSECT",VERTEX,{"disambiguationData":[OD(0.0)],"derivedFrom":[subQ1,subQ4]});Q0=makeQuery(id+"F0.imprint","IMPRINT",FACE,{"disambiguationData":[TD([[makeQuery(id+"F0.imprint","IMPRINT",EDGE,{"disambiguationData":[TD([[subQ9,-1.0]])],"derivedFrom":subQ1}),-1.0]])]});}
            var Q1;
            {var subQ0=sQuery(id+"F0.wireOp",EDGE,"E41");var subQ1=sQuery(id+"F0.wireOp",EDGE,"E17");var subQ2=makeQuery(id+"F0.imprint","INTERSECT",VERTEX,{"disambiguationData":[OD(0.0)],"derivedFrom":[subQ1,subQ0]});Q1=makeQuery(id+"F0.imprint","IMPRINT",FACE,{"disambiguationData":[TD([[makeQuery(id+"F0.imprint","IMPRINT",EDGE,{"disambiguationData":[TD([[subQ2,-1.0]])],"derivedFrom":subQ1}),-1.0]])]});}
            var Q2;
            {var subQ1=sQuery(id+"F0.wireOp",EDGE,"E5");var subQ7=sQuery(id+"F0.wireOp",EDGE,"E41");var subQ8=makeQuery(id+"F0.imprint","INTERSECT",VERTEX,{"disambiguationData":[OD(0.0)],"derivedFrom":[subQ1,subQ7]});Q2=makeQuery(id+"F0.imprint","IMPRINT",FACE,{"disambiguationData":[TD([[makeQuery(id+"F0.imprint","IMPRINT",EDGE,{"disambiguationData":[TD([[subQ8,-1.0]])],"derivedFrom":subQ1}),-1.0]])]});}
            var Q3;
            {var subQ3=sQuery(id+"F0.wireOp",EDGE,"E15");var subQ5=sQuery(id+"F0.wireOp",EDGE,"E5");var subQ6=makeQuery(id+"F0.imprint","INTERSECT",VERTEX,{"derivedFrom":[subQ5,subQ3]});Q3=makeQuery(id+"F0.imprint","IMPRINT",FACE,{"disambiguationData":[TD([[makeQuery(id+"F0.imprint","IMPRINT",EDGE,{"disambiguationData":[TD([[subQ6,-1.0]])],"derivedFrom":subQ5}),-1.0]])]});}
            var Q4;
            {var subQ0=sQuery(id+"F0.wireOp",EDGE,"E42");var subQ1=sQuery(id+"F0.wireOp",EDGE,"E5");var subQ2=makeQuery(id+"F0.imprint","INTERSECT",VERTEX,{"disambiguationData":[OD(0.0)],"derivedFrom":[subQ1,subQ0]});Q4=makeQuery(id+"F0.imprint","IMPRINT",FACE,{"disambiguationData":[TD([[makeQuery(id+"F0.imprint","IMPRINT",EDGE,{"disambiguationData":[TD([[subQ2,-1.0]])],"derivedFrom":subQ1}),1.0]])]});}
            var Q5;
            {var subQ4=sQuery(id+"F0.wireOp",EDGE,"E42");var subQ5=sQuery(id+"F0.wireOp",EDGE,"E5");var subQ6=makeQuery(id+"F0.imprint","INTERSECT",VERTEX,{"disambiguationData":[OD(0.0)],"derivedFrom":[subQ5,subQ4]});Q5=makeQuery(id+"F0.imprint","IMPRINT",FACE,{"disambiguationData":[TD([[makeQuery(id+"F0.imprint","IMPRINT",EDGE,{"disambiguationData":[TD([[subQ6,-1.0]])],"derivedFrom":subQ5}),-1.0]])]});}
            var Q6;
            {var subQ1=sQuery(id+"F0.wireOp",EDGE,"E10");var subQ4=sQuery(id+"F0.wireOp",EDGE,"E42");var subQ9=makeQuery(id+"F0.imprint","INTERSECT",VERTEX,{"disambiguationData":[OD(0.0)],"derivedFrom":[subQ1,subQ4]});Q6=makeQuery(id+"F0.imprint","IMPRINT",FACE,{"disambiguationData":[TD([[makeQuery(id+"F0.imprint","IMPRINT",EDGE,{"disambiguationData":[TD([[subQ9,-1.0]])],"derivedFrom":subQ1}),-1.0]])]});}
            var Q7;
            {var subQ0=sQuery(id+"F0.wireOp",EDGE,"E42");var subQ1=sQuery(id+"F0.wireOp",EDGE,"E17");var subQ2=makeQuery(id+"F0.imprint","INTERSECT",VERTEX,{"disambiguationData":[OD(0.0)],"derivedFrom":[subQ1,subQ0]});Q7=makeQuery(id+"F0.imprint","IMPRINT",FACE,{"disambiguationData":[TD([[makeQuery(id+"F0.imprint","IMPRINT",EDGE,{"disambiguationData":[TD([[subQ2,-1.0]])],"derivedFrom":subQ1}),-1.0]])]});}
            var Q8;
            {var subQ0=sQuery(id+"F0.wireOp",EDGE,"E44");var subQ1=sQuery(id+"F0.wireOp",EDGE,"E17");var subQ2=makeQuery(id+"F0.imprint","INTERSECT",VERTEX,{"disambiguationData":[OD(0.0)],"derivedFrom":[subQ1,subQ0]});Q8=makeQuery(id+"F0.imprint","IMPRINT",FACE,{"disambiguationData":[TD([[makeQuery(id+"F0.imprint","IMPRINT",EDGE,{"disambiguationData":[TD([[subQ2,-1.0]])],"derivedFrom":subQ1}),-1.0]])]});}
            var Q9;
            {var subQ1=sQuery(id+"F0.wireOp",EDGE,"E10");var subQ4=sQuery(id+"F0.wireOp",EDGE,"E44");var subQ9=makeQuery(id+"F0.imprint","INTERSECT",VERTEX,{"disambiguationData":[OD(0.0)],"derivedFrom":[subQ1,subQ4]});Q9=makeQuery(id+"F0.imprint","IMPRINT",FACE,{"disambiguationData":[TD([[makeQuery(id+"F0.imprint","IMPRINT",EDGE,{"disambiguationData":[TD([[subQ9,-1.0]])],"derivedFrom":subQ1}),-1.0]])]});}
            var Q10;
            {var subQ5=sQuery(id+"F0.wireOp",EDGE,"E5");var subQ7=sQuery(id+"F0.wireOp",EDGE,"E44");var subQ9=makeQuery(id+"F0.imprint","INTERSECT",VERTEX,{"disambiguationData":[OD(0.0)],"derivedFrom":[subQ5,subQ7]});Q10=makeQuery(id+"F0.imprint","IMPRINT",FACE,{"disambiguationData":[TD([[makeQuery(id+"F0.imprint","IMPRINT",EDGE,{"disambiguationData":[TD([[subQ9,-1.0]])],"derivedFrom":subQ5}),-1.0]])]});}
            var Q11;
            {var subQ3=sQuery(id+"F0.wireOp",EDGE,"E16");var subQ7=sQuery(id+"F0.wireOp",EDGE,"E5");var subQ8=makeQuery(id+"F0.imprint","INTERSECT",VERTEX,{"derivedFrom":[subQ7,subQ3]});Q11=makeQuery(id+"F0.imprint","IMPRINT",FACE,{"disambiguationData":[TD([[makeQuery(id+"F0.imprint","IMPRINT",EDGE,{"disambiguationData":[TD([[subQ8,-1.0]])],"derivedFrom":subQ7}),-1.0]])]});}
            var Q12;
            {var subQ0=sQuery(id+"F0.wireOp",EDGE,"E16");var subQ1=sQuery(id+"F0.wireOp",EDGE,"E5");var subQ2=makeQuery(id+"F0.imprint","INTERSECT",VERTEX,{"derivedFrom":[subQ1,subQ0]});Q12=makeQuery(id+"F0.imprint","IMPRINT",FACE,{"disambiguationData":[TD([[makeQuery(id+"F0.imprint","IMPRINT",EDGE,{"disambiguationData":[TD([[subQ2,-1.0]])],"derivedFrom":subQ1}),1.0]])]});}
            var Q13;
            {var subQ0=sQuery(id+"F0.wireOp",EDGE,"E44");var subQ1=sQuery(id+"F0.wireOp",EDGE,"E5");var subQ2=makeQuery(id+"F0.imprint","INTERSECT",VERTEX,{"disambiguationData":[OD(0.0)],"derivedFrom":[subQ1,subQ0]});Q13=makeQuery(id+"F0.imprint","IMPRINT",FACE,{"disambiguationData":[TD([[makeQuery(id+"F0.imprint","IMPRINT",EDGE,{"disambiguationData":[TD([[subQ2,-1.0]])],"derivedFrom":subQ1}),1.0]])]});}
            var Q14;
            {var subQ0=sQuery(id+"F0.wireOp",EDGE,"E43");var subQ1=sQuery(id+"F0.wireOp",EDGE,"E5");var subQ2=makeQuery(id+"F0.imprint","INTERSECT",VERTEX,{"disambiguationData":[OD(0.0)],"derivedFrom":[subQ1,subQ0]});Q14=makeQuery(id+"F0.imprint","IMPRINT",FACE,{"disambiguationData":[TD([[makeQuery(id+"F0.imprint","IMPRINT",EDGE,{"disambiguationData":[TD([[subQ2,1.0]])],"derivedFrom":subQ1}),1.0]])]});}
            var Q15;
            {var subQ4=sQuery(id+"F0.wireOp",EDGE,"E43");var subQ6=sQuery(id+"F0.wireOp",EDGE,"E5");var subQ7=makeQuery(id+"F0.imprint","INTERSECT",VERTEX,{"disambiguationData":[OD(0.0)],"derivedFrom":[subQ6,subQ4]});Q15=makeQuery(id+"F0.imprint","IMPRINT",FACE,{"disambiguationData":[TD([[makeQuery(id+"F0.imprint","IMPRINT",EDGE,{"disambiguationData":[TD([[subQ7,1.0]])],"derivedFrom":subQ6}),-1.0]])]});}
            var Q16;
            {var subQ1=sQuery(id+"F0.wireOp",EDGE,"E10");var subQ4=sQuery(id+"F0.wireOp",EDGE,"E43");var subQ9=makeQuery(id+"F0.imprint","INTERSECT",VERTEX,{"disambiguationData":[OD(0.0)],"derivedFrom":[subQ1,subQ4]});Q16=makeQuery(id+"F0.imprint","IMPRINT",FACE,{"disambiguationData":[TD([[makeQuery(id+"F0.imprint","IMPRINT",EDGE,{"disambiguationData":[TD([[subQ9,1.0]])],"derivedFrom":subQ1}),-1.0]])]});}
            var Q17;
            {var subQ0=sQuery(id+"F0.wireOp",EDGE,"E43");var subQ1=sQuery(id+"F0.wireOp",EDGE,"E17");var subQ2=makeQuery(id+"F0.imprint","INTERSECT",VERTEX,{"disambiguationData":[OD(0.0)],"derivedFrom":[subQ1,subQ0]});Q17=makeQuery(id+"F0.imprint","IMPRINT",FACE,{"disambiguationData":[TD([[makeQuery(id+"F0.imprint","IMPRINT",EDGE,{"disambiguationData":[TD([[subQ2,1.0]])],"derivedFrom":subQ1}),-1.0]])]});}
            extrude(context, id + "F11", {"entities" : qUnion([Q0, Q1, Q2, Q3, Q4, Q5, Q6, Q7, Q8, Q9, Q10, Q11, Q12, Q13, Q14, Q15, Q16, Q17]), "operationType" : NewBodyOperationType.REMOVE, "depth" : 1.5 * mm});
        }
        {
            var Q0;
            Q0=makeQuery(id+"F1.opExtrude","SWEPT_FACE",FACE,{"disambiguationData":[OSD([sQuery(id+"F0.wireOp",EDGE,"E0.bottom")])]});
            var sketch = newSketch(context, id + "F12", { "sketchPlane" : qUnion([Q0])});
            skLineSegment(sketch, "E45", {"start": v(35, -9) * mm, "end": v(-12.5, -9) * mm});
            skLineSegment(sketch, "E46.0", {"start": v(35, -11) * mm, "end": v(-13, -11) * mm});
            skSolve(sketch);
        }
        {
            var Q0;
            {var subQ0=sQuery(id+"F12.wireOp",EDGE,"E45");Q0=makeQuery(id+"F12.imprint","IMPRINT",FACE,{"disambiguationData":[TD([[makeQuery(id+"F12.imprint","IMPRINT",EDGE,{"derivedFrom":subQ0}),1.0]])]});}
            extrude(context, id + "F13", {"entities" : qUnion([Q0]), "operationType" : NewBodyOperationType.REMOVE, "oppositeDirection" : true, "depth" : 1 * mm});
        }
        {
            var Q0;
            Q0=makeQuery(id+"F1.opExtrude","SWEPT_FACE",FACE,{"disambiguationData":[OSD([sQuery(id+"F0.wireOp",EDGE,"E0.top")])]});
            var sketch = newSketch(context, id + "F14", { "sketchPlane" : qUnion([Q0])});
            skLineSegment(sketch, "E47", {"start": v(-35, -11) * mm, "end": v(12.5, -11) * mm});
            skLineSegment(sketch, "E48.0", {"start": v(-35, -9) * mm, "end": v(13, -9) * mm});
            skSolve(sketch);
        }
        {
            var Q0;
            {var subQ0=sQuery(id+"F14.wireOp",EDGE,"E47");Q0=makeQuery(id+"F14.imprint","IMPRINT",FACE,{"disambiguationData":[TD([[makeQuery(id+"F14.imprint","IMPRINT",EDGE,{"derivedFrom":subQ0}),1.0]])]});}
            extrude(context, id + "F15", {"entities" : qUnion([Q0]), "operationType" : NewBodyOperationType.REMOVE, "oppositeDirection" : true, "depth" : 1 * mm});
        }
        {
            var Q0;
            {var subQ0=sQuery(id+"F0.wireOp",EDGE,"E26");var subQ1=sQuery(id+"F0.wireOp",EDGE,"E25");Q0=makeQuery(id+"F4.opFillet","BLEND_EDGE",EDGE,{"blendedFrom":[makeQuery(id+"F3.opExtrude","SWEPT_EDGE",EDGE,{"disambiguationData":[OSD([subQ1,subQ0])]}),makeQuery(id+"F3.opExtrude","CAP_FACE",FACE,{"disambiguationData":[OSD([sQuery(id+"F0.wireOp",EDGE,"E0.right"),sQuery(id+"F0.wireOp",EDGE,"E4"),sQuery(id+"F0.wireOp",EDGE,"E22"),sQuery(id+"F0.wireOp",EDGE,"E23"),sQuery(id+"F0.wireOp",EDGE,"E24"),subQ1,subQ0,sQuery(id+"F0.wireOp",EDGE,"E27"),sQuery(id+"F0.wireOp",EDGE,"E28"),sQuery(id+"F0.wireOp",EDGE,"E41"),sQuery(id+"F0.wireOp",EDGE,"E42"),sQuery(id+"F0.wireOp",EDGE,"E43"),sQuery(id+"F0.wireOp",EDGE,"E44")])],"isStart":false})],"blendedInto":[makeQuery(id+"F3.opExtrude","CAP_FACE",FACE,{"disambiguationData":[OSD([sQuery(id+"F0.wireOp",EDGE,"E0.right"),sQuery(id+"F0.wireOp",EDGE,"E4"),sQuery(id+"F0.wireOp",EDGE,"E22"),sQuery(id+"F0.wireOp",EDGE,"E23"),sQuery(id+"F0.wireOp",EDGE,"E24"),subQ1,subQ0,sQuery(id+"F0.wireOp",EDGE,"E27"),sQuery(id+"F0.wireOp",EDGE,"E28"),sQuery(id+"F0.wireOp",EDGE,"E41"),sQuery(id+"F0.wireOp",EDGE,"E42"),sQuery(id+"F0.wireOp",EDGE,"E43"),sQuery(id+"F0.wireOp",EDGE,"E44")])],"isStart":false})]});}
            var Q1;
            Q1=makeQuery(id+"F3.opExtrude","CAP_EDGE",EDGE,{"disambiguationData":[OSD([sQuery(id+"F0.wireOp",EDGE,"E0.right"),sQuery(id+"F0.wireOp",EDGE,"E22"),sQuery(id+"F0.wireOp",EDGE,"E25")])],"isStart":false});
            var Q2;
            {var subQ0=sQuery(id+"F0.wireOp",EDGE,"E23");var subQ1=sQuery(id+"F0.wireOp",EDGE,"E22");Q2=makeQuery(id+"F4.opFillet","BLEND_EDGE",EDGE,{"blendedFrom":[makeQuery(id+"F3.opExtrude","SWEPT_EDGE",EDGE,{"disambiguationData":[OSD([subQ1,subQ0])]}),makeQuery(id+"F3.opExtrude","CAP_FACE",FACE,{"disambiguationData":[OSD([sQuery(id+"F0.wireOp",EDGE,"E0.right"),sQuery(id+"F0.wireOp",EDGE,"E4"),subQ1,subQ0,sQuery(id+"F0.wireOp",EDGE,"E24"),sQuery(id+"F0.wireOp",EDGE,"E25"),sQuery(id+"F0.wireOp",EDGE,"E26"),sQuery(id+"F0.wireOp",EDGE,"E27"),sQuery(id+"F0.wireOp",EDGE,"E28"),sQuery(id+"F0.wireOp",EDGE,"E41"),sQuery(id+"F0.wireOp",EDGE,"E42"),sQuery(id+"F0.wireOp",EDGE,"E43"),sQuery(id+"F0.wireOp",EDGE,"E44")])],"isStart":false})],"blendedInto":[makeQuery(id+"F3.opExtrude","CAP_FACE",FACE,{"disambiguationData":[OSD([sQuery(id+"F0.wireOp",EDGE,"E0.right"),sQuery(id+"F0.wireOp",EDGE,"E4"),subQ1,subQ0,sQuery(id+"F0.wireOp",EDGE,"E24"),sQuery(id+"F0.wireOp",EDGE,"E25"),sQuery(id+"F0.wireOp",EDGE,"E26"),sQuery(id+"F0.wireOp",EDGE,"E27"),sQuery(id+"F0.wireOp",EDGE,"E28"),sQuery(id+"F0.wireOp",EDGE,"E41"),sQuery(id+"F0.wireOp",EDGE,"E42"),sQuery(id+"F0.wireOp",EDGE,"E43"),sQuery(id+"F0.wireOp",EDGE,"E44")])],"isStart":false})]});}
            var Q3;
            {var subQ0=sQuery(id+"F0.wireOp",EDGE,"E0.bottom");var subQ1=sQuery(id+"F0.wireOp",EDGE,"E0.left");Q3=makeQuery(id+"F13.boolean.opBoolean","SPLIT",EDGE,{"disambiguationData":[TD([makeQuery(id+"F13.opExtrude","SWEPT_FACE",FACE,{"disambiguationData":[OSD([sQuery(id+"F12.wireOp",EDGE,"E45")])]})])],"derivedFrom":makeQuery(id+"F1.opExtrude","SWEPT_EDGE",EDGE,{"disambiguationData":[OSD([subQ0,subQ1])]})});}
            var Q4;
            Q4=makeQuery(id+"F13.boolean.opBoolean","COPY",EDGE,{"derivedFrom":makeQuery(id+"F13.opExtrude","CAP_EDGE",EDGE,{"disambiguationData":[OSD([sQuery(id+"F0.wireOp",EDGE,"E0.bottom"),sQuery(id+"F0.wireOp",EDGE,"E0.left")])],"isStart":false})});
            var Q5;
            {var subQ0=sQuery(id+"F0.wireOp",EDGE,"E0.bottom");var subQ1=sQuery(id+"F0.wireOp",EDGE,"E0.left");Q5=makeQuery(id+"F13.boolean.opBoolean","SPLIT",EDGE,{"disambiguationData":[TD([makeQuery(id+"F13.opExtrude","SWEPT_FACE",FACE,{"disambiguationData":[OSD([sQuery(id+"F12.wireOp",EDGE,"E46.0")])]})])],"derivedFrom":makeQuery(id+"F1.opExtrude","SWEPT_EDGE",EDGE,{"disambiguationData":[OSD([subQ0,subQ1])]})});}
            var Q6;
            {var subQ0=sQuery(id+"F0.wireOp",EDGE,"E0.left");var subQ1=sQuery(id+"F0.wireOp",EDGE,"E0.top");Q6=makeQuery(id+"F15.boolean.opBoolean","SPLIT",EDGE,{"disambiguationData":[TD([makeQuery(id+"F15.opExtrude","SWEPT_FACE",FACE,{"disambiguationData":[OSD([sQuery(id+"F14.wireOp",EDGE,"E47")])]})])],"derivedFrom":makeQuery(id+"F1.opExtrude","SWEPT_EDGE",EDGE,{"disambiguationData":[OSD([subQ1,subQ0])]})});}
            var Q7;
            Q7=makeQuery(id+"F15.boolean.opBoolean","COPY",EDGE,{"derivedFrom":makeQuery(id+"F15.opExtrude","CAP_EDGE",EDGE,{"disambiguationData":[OSD([sQuery(id+"F0.wireOp",EDGE,"E0.top"),sQuery(id+"F0.wireOp",EDGE,"E0.left")])],"isStart":false})});
            var Q8;
            {var subQ0=sQuery(id+"F0.wireOp",EDGE,"E0.left");var subQ1=sQuery(id+"F0.wireOp",EDGE,"E0.top");Q8=makeQuery(id+"F15.boolean.opBoolean","SPLIT",EDGE,{"disambiguationData":[TD([makeQuery(id+"F15.opExtrude","SWEPT_FACE",FACE,{"disambiguationData":[OSD([sQuery(id+"F14.wireOp",EDGE,"E48.0")])]})])],"derivedFrom":makeQuery(id+"F1.opExtrude","SWEPT_EDGE",EDGE,{"disambiguationData":[OSD([subQ1,subQ0])]})});}
            var Q9;
            Q9=makeQuery(id+"F1.opExtrude","CAP_EDGE",EDGE,{"disambiguationData":[OSD([sQuery(id+"F0.wireOp",EDGE,"E0.bottom")])],"isStart":true});
            var Q10;
            Q10=makeQuery(id+"F1.opExtrude","CAP_EDGE",EDGE,{"disambiguationData":[OSD([sQuery(id+"F0.wireOp",EDGE,"E0.top")])],"isStart":true});
            var Q11;
            {var subQ0=sQuery(id+"F0.wireOp",EDGE,"E29");Q11=makeQuery(id+"F9.boolean.opBoolean","MERGE",EDGE,{"derivedFrom":[makeQuery(id+"F2.boolean.opBoolean","COPY",EDGE,{"derivedFrom":makeQuery(id+"F2.opExtrude","CAP_EDGE",EDGE,{"disambiguationData":[OSD([subQ0])],"isStart":true})}),makeQuery(id+"F9.opExtrude","CAP_EDGE",EDGE,{"disambiguationData":[OSD([subQ0]),TDD([makeQuery(id+"F0.imprint","IMPRINT",EDGE,{"disambiguationData":[TD([[makeQuery(id+"F0.imprint","INTERSECT",VERTEX,{"derivedFrom":[sQuery(id+"F0.wireOp",EDGE,"E9.right"),subQ0]}),1.0]])],"derivedFrom":subQ0})])],"isStart":true})]});}
            var Q12;
            {var subQ0=sQuery(id+"F0.wireOp",EDGE,"E30");Q12=makeQuery(id+"F9.boolean.opBoolean","MERGE",EDGE,{"derivedFrom":[makeQuery(id+"F2.boolean.opBoolean","COPY",EDGE,{"derivedFrom":makeQuery(id+"F2.opExtrude","CAP_EDGE",EDGE,{"disambiguationData":[OSD([subQ0])],"isStart":true})}),makeQuery(id+"F9.opExtrude","CAP_EDGE",EDGE,{"disambiguationData":[OSD([subQ0]),TDD([makeQuery(id+"F0.imprint","IMPRINT",EDGE,{"disambiguationData":[TD([[makeQuery(id+"F0.imprint","INTERSECT",VERTEX,{"derivedFrom":[sQuery(id+"F0.wireOp",EDGE,"E9.right"),subQ0]}),1.0]])],"derivedFrom":subQ0})])],"isStart":true})]});}
            var Q13;
            {var subQ0=sQuery(id+"F0.wireOp",EDGE,"E29");Q13=makeQuery(id+"F9.boolean.opBoolean","COPY",EDGE,{"derivedFrom":makeQuery(id+"F9.opExtrude","CAP_EDGE",EDGE,{"disambiguationData":[OSD([subQ0]),TDD([makeQuery(id+"F0.imprint","IMPRINT",EDGE,{"disambiguationData":[TD([[makeQuery(id+"F0.imprint","INTERSECT",VERTEX,{"derivedFrom":[sQuery(id+"F0.wireOp",EDGE,"E7"),subQ0]}),1.0]])],"derivedFrom":subQ0})])],"isStart":true})});}
            var Q14;
            {var subQ0=sQuery(id+"F0.wireOp",EDGE,"E30");Q14=makeQuery(id+"F9.boolean.opBoolean","COPY",EDGE,{"derivedFrom":makeQuery(id+"F9.opExtrude","CAP_EDGE",EDGE,{"disambiguationData":[OSD([subQ0]),TDD([makeQuery(id+"F0.imprint","IMPRINT",EDGE,{"disambiguationData":[TD([[makeQuery(id+"F0.imprint","INTERSECT",VERTEX,{"derivedFrom":[sQuery(id+"F0.wireOp",EDGE,"E7"),subQ0]}),1.0]])],"derivedFrom":subQ0})])],"isStart":true})});}
            var Q15;
            {var subQ0=sQuery(id+"F0.wireOp",EDGE,"E9.right");var subQ1=sQuery(id+"F0.wireOp",EDGE,"E30");Q15=makeQuery(id+"F9.boolean.opBoolean","SPLIT",EDGE,{"disambiguationData":[TD([makeQuery(id+"F2.boolean.opBoolean","COPY",FACE,{"derivedFrom":makeQuery(id+"F2.opExtrude","SWEPT_FACE",FACE,{"disambiguationData":[OSD([subQ1])]})})])],"derivedFrom":makeQuery(id+"F7.boolean.opBoolean","COPY",EDGE,{"derivedFrom":makeQuery(id+"F7.opExtrude","CAP_EDGE",EDGE,{"disambiguationData":[OSD([subQ0])],"isStart":true})})});}
            var Q16;
            {var subQ0=sQuery(id+"F0.wireOp",EDGE,"E9.right");var subQ1=sQuery(id+"F0.wireOp",EDGE,"E29");Q16=makeQuery(id+"F9.boolean.opBoolean","SPLIT",EDGE,{"disambiguationData":[TD([makeQuery(id+"F2.boolean.opBoolean","COPY",FACE,{"derivedFrom":makeQuery(id+"F2.opExtrude","SWEPT_FACE",FACE,{"disambiguationData":[OSD([subQ1])]})})])],"derivedFrom":makeQuery(id+"F7.boolean.opBoolean","COPY",EDGE,{"derivedFrom":makeQuery(id+"F7.opExtrude","CAP_EDGE",EDGE,{"disambiguationData":[OSD([subQ0])],"isStart":true})})});}
            var Q17;
            Q17=makeQuery(id+"F7.boolean.opBoolean","COPY",EDGE,{"derivedFrom":makeQuery(id+"F7.opExtrude","CAP_EDGE",EDGE,{"disambiguationData":[OSD([sQuery(id+"F0.wireOp",EDGE,"E9.top")])],"isStart":true})});
            var Q18;
            {var subQ1=sQuery(id+"F0.wireOp",EDGE,"E9.left");Q18=makeQuery(id+"F9.boolean.opBoolean","SPLIT",EDGE,{"disambiguationData":[TD([makeQuery(id+"F7.boolean.opBoolean","COPY",FACE,{"derivedFrom":makeQuery(id+"F7.opExtrude","SWEPT_FACE",FACE,{"disambiguationData":[OSD([sQuery(id+"F0.wireOp",EDGE,"E9.top")])]})})])],"derivedFrom":makeQuery(id+"F7.boolean.opBoolean","COPY",EDGE,{"derivedFrom":makeQuery(id+"F7.opExtrude","CAP_EDGE",EDGE,{"disambiguationData":[OSD([subQ1])],"isStart":true})})});}
            var Q19;
            {var subQ1=sQuery(id+"F0.wireOp",EDGE,"E9.left");Q19=makeQuery(id+"F9.boolean.opBoolean","SPLIT",EDGE,{"disambiguationData":[TD([makeQuery(id+"F7.boolean.opBoolean","COPY",FACE,{"derivedFrom":makeQuery(id+"F7.opExtrude","SWEPT_FACE",FACE,{"disambiguationData":[OSD([sQuery(id+"F0.wireOp",EDGE,"E9.bottom")])]})})])],"derivedFrom":makeQuery(id+"F7.boolean.opBoolean","COPY",EDGE,{"derivedFrom":makeQuery(id+"F7.opExtrude","CAP_EDGE",EDGE,{"disambiguationData":[OSD([subQ1])],"isStart":true})})});}
            var Q20;
            Q20=makeQuery(id+"F7.boolean.opBoolean","COPY",EDGE,{"derivedFrom":makeQuery(id+"F7.opExtrude","CAP_EDGE",EDGE,{"disambiguationData":[OSD([sQuery(id+"F0.wireOp",EDGE,"E9.bottom")])],"isStart":true})});
            var Q21;
            {var subQ0=sQuery(id+"F0.wireOp",EDGE,"E7");Q21=makeQuery(id+"F9.boolean.opBoolean","MERGE",EDGE,{"derivedFrom":[makeQuery(id+"F8.boolean.opBoolean","COPY",EDGE,{"derivedFrom":makeQuery(id+"F8.opExtrude","CAP_EDGE",EDGE,{"disambiguationData":[OSD([subQ0])],"isStart":true})}),makeQuery(id+"F9.opExtrude","CAP_EDGE",EDGE,{"disambiguationData":[OSD([subQ0]),TDD([makeQuery(id+"F0.imprint","IMPRINT",EDGE,{"disambiguationData":[TD([[makeQuery(id+"F0.imprint","INTERSECT",VERTEX,{"derivedFrom":[sQuery(id+"F0.wireOp",EDGE,"E1.top"),subQ0]}),-1.0]])],"derivedFrom":subQ0})])],"isStart":true})]});}
            var Q22;
            {var subQ0=sQuery(id+"F0.wireOp",EDGE,"E7");Q22=makeQuery(id+"F9.boolean.opBoolean","MERGE",EDGE,{"derivedFrom":[makeQuery(id+"F8.boolean.opBoolean","COPY",EDGE,{"derivedFrom":makeQuery(id+"F8.opExtrude","CAP_EDGE",EDGE,{"disambiguationData":[OSD([subQ0])],"isStart":true})}),makeQuery(id+"F9.opExtrude","CAP_EDGE",EDGE,{"disambiguationData":[OSD([subQ0]),TDD([makeQuery(id+"F0.imprint","IMPRINT",EDGE,{"disambiguationData":[TD([[makeQuery(id+"F0.imprint","INTERSECT",VERTEX,{"derivedFrom":[sQuery(id+"F0.wireOp",EDGE,"E2.bottom"),subQ0]}),1.0]])],"derivedFrom":subQ0})])],"isStart":true})]});}
            fillet(context, id + "F16", {"entities" : qUnion([Q0, Q1, Q2, Q3, Q4, Q5, Q6, Q7, Q8, Q9, Q10, Q11, Q12, Q13, Q14, Q15, Q16, Q17, Q18, Q19, Q20, Q21, Q22]), "radius" : 0.5 * mm, "tangentPropagation" : true, "allowEdgeOverflow" : false});
        }
        {
            var Q0;
            {var subQ0=sQuery(id+"F0.wireOp",EDGE,"E39");Q0=makeQuery(id+"F0.imprint","IMPRINT",FACE,{"disambiguationData":[TD([[makeQuery(id+"F0.imprint","IMPRINT",EDGE,{"derivedFrom":subQ0}),-1.0]])]});}
            extrude(context, id + "F17", {"entities" : qUnion([Q0]), "operationType" : NewBodyOperationType.REMOVE, "oppositeDirection" : true, "depth" : 5 * mm});
        }
        {
            var Q0;
            Q0=makeQuery(id+"F10.opExtrude","CAP_EDGE",EDGE,{"disambiguationData":[OSD([sQuery(id+"F0.wireOp",EDGE,"E20")])],"isStart":false});
            var Q1;
            Q1=makeQuery(id+"F10.opExtrude","CAP_EDGE",EDGE,{"disambiguationData":[OSD([sQuery(id+"F0.wireOp",EDGE,"E18")])],"isStart":false});
            var Q2;
            Q2=makeQuery(id+"F10.opExtrude","CAP_EDGE",EDGE,{"disambiguationData":[OSD([sQuery(id+"F0.wireOp",EDGE,"E19")])],"isStart":false});
            var Q3;
            Q3=makeQuery(id+"F10.opExtrude","CAP_EDGE",EDGE,{"disambiguationData":[OSD([sQuery(id+"F0.wireOp",EDGE,"E21")])],"isStart":false});
            fillet(context, id + "F18", {"entities" : qUnion([Q0, Q1, Q2, Q3]), "radius" : 1 * mm, "tangentPropagation" : true, "allowEdgeOverflow" : false});
        }
    });
